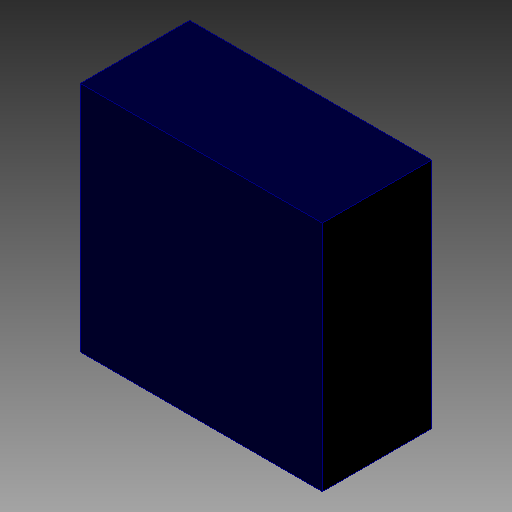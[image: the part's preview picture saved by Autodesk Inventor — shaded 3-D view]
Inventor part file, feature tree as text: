
AUTODESK INVENTOR PART (.ipt)
format: ipt  version: 2018 (Build 220112000, 112)  size: 80,896 bytes
history: native  units: in
note: dims shown in document units (in); Inventor stores cm internally (conversion verified against a paired STEP export)
features: other x1, extrude x1
ambient origin geometry x8: Origin, YZ Plane, XZ Plane, XY Plane, X Axis, Y Axis, Z Axis, Center Point
bodies: Solid1 (feature_tree)
feature tree (2):
  other  "TILOGO_SMALL, U_2_TILOGO_SMALL_156"
  extrude  "Extrusion1"  Depth=0.0394in TaperAngle=0.0deg
